# Revit family: QF_ELECTROLUXPROFESSIONAL_1LSNJ4_IC64821_E
name_source: partatom
category: Attrezzature speciali
units: mm (PartAtom-declared; Revit-internal decimal feet)

## family parameters
Basato su piano di lavoro = No
Condiviso = No
Punto di calcolo locali = No
Quota connettore circolare = Usa diametro
Sempre verticale = Sì
Taglio con vuoti quando caricato = No
Tipo di parte = Normale

## types (11) — shared parameters
Cycle = 50 Hz
Depth Actual = 1110 mm  [stored 3.64173 ft]
Height Actual = 1270 mm  [stored 4.16667 ft]
Latent Heat Output = 0.0
Length Actual = 2775 mm  [stored 9.10433 ft]
Modello = IC64821
Phase = 3
Produttore = Electrolux Professional
Sensible Heat Output = 0.0
URL = www.electroluxprofessional.com
Volts = 400 V
Weight = 945
zero-valued in all types: Gas KW, Prospetto di default, Steam Pounds per Hour

## per-type parameters (varying)
| type | Descrizione | Item Number | Watts |
| 9882030155 | IRONER CYLINDER IC64821 2120MM EL. CE 400/50/3 6MM SST CYL. FR VAC.FEED.TABLE | 1L0GSB | 37700 W |
| 9882030251 | IRONER CYLINDER IC64821 2120MM PERFORMANCE EL. CE 400/50/3 DUBIXIUM FR VAC.FEED.TABLE | 1L0GYK | 37700 W |
| 9882030206 | IRONER CYLINDER IC64821 2120MM ACTIVE EL. CE 400/50/3 6MM SST CYL. FR FEED NOW | 1L8275 | 37700 W |
| 9882030207 | IRONER CYLINDER IC64821 2120MM ACTIVE EL. CE 400/50/3 6MM SST CYL. ML FEED NOW | 1L8276 | 37700 W |
| 9882030217 | IRONER CYLINDER IC64821 2120MM EL. CE 400/50/3 DUBIXIUM NO VAC.FEED.TABLE DIAMMS | 1L0GU5 | 37700 W |
| 9882030304 | IRONER CYLINDER IC64821 2120MM EL. CE 400/50/3 DUBIXIUM NOR VAC.FEED.TABLE ANTISTATIC DIAMMS | 1LT670 | 377000 W |
| 9882030286 | IRONER CYLINDER IC64821 2120MM SUPERIOR EL. CE 400/50/3 DUBIXIUM FR FEED ALONE VAC.FEED.TABLE | 1L0H8M | 37700 W |
| 9882030258 | IRONER CYLINDER IC64821 2120MM PERFORMANCE EL. CE 400/50/3 DUBIXIUM ML VAC.FEED.TABLE | 1L0H1R | 37700 W |
| 9882030252 | IRONER CYLINDER IC64821 2120MM SUPERIOR EL. CE 400/50/3 DUBIXIUM ML FEED ALONE VAC.FEED.TABLE | 1LSPEH | 37700 W |
| 9882030320 | IRONER CYLINDER IC64821 2120MM EL. CE 400/50/3 6MM SST CYL. SE, DK, FI VAC.FEED.TABLE ANTISTATIC DIAMMS | 1LT6KU | 37700 W |
| 9882030154 | IRONER CYLINDER IC64821 2120MM EL. CE 400/50/3 6MM SST CYL. ML VAC.FEED.TABLE | 1L0GSA | 37700 W |

note: [stored X ft] marks values corroborated as IEEE doubles in the binary element streams (Revit-internal decimal feet)

## geometry (parser evidence)
native form markers: Sweep x11
no freeform markers — native parametric forms only
